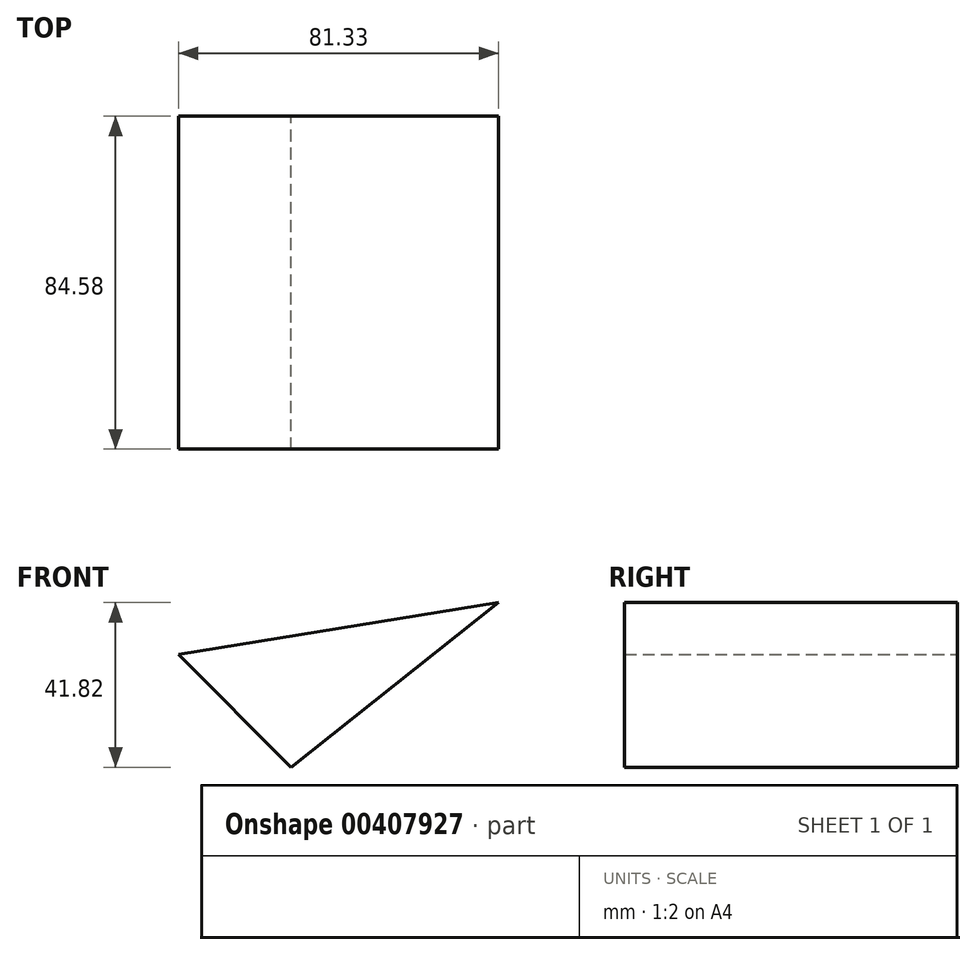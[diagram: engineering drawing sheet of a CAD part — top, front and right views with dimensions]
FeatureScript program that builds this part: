
annotation { "Feature Type Name" : "Feature", "Feature Type Description" : "" }
export const myFeature = defineFeature(function(context is Context, id is Id, definition is map)
    precondition{}
    {
        {
            var Q0;
            Q0=qCreatedBy(makeId("Front.planeOp"),FACE);
            var sketch = newSketch(context, id + "F0", { "sketchPlane" : qUnion([Q0])});
            skLineSegment(sketch, "E0", {"start": v(-96.78, 61.4) * mm, "end": v(-68.24, 32.69) * mm});
            skLineSegment(sketch, "E1", {"start": v(-68.24, 32.69) * mm, "end": v(-15.45, 74.51) * mm});
            skLineSegment(sketch, "E2", {"start": v(-15.45, 74.51) * mm, "end": v(-96.78, 61.4) * mm});
            skSolve(sketch);
        }
        {
            var Q0;
            Q0=makeQuery(id+"F0.imprint","IMPRINT",FACE,{"disambiguationData":[TD([[makeQuery(id+"F0.imprint","IMPRINT",EDGE,{"derivedFrom":sQuery(id+"F0.wireOp",EDGE,"E0")}),1.0]])]});
            extrude(context, id + "F1", {"entities" : qUnion([Q0]), "depth" : 84.58 * mm});
        }
    });
